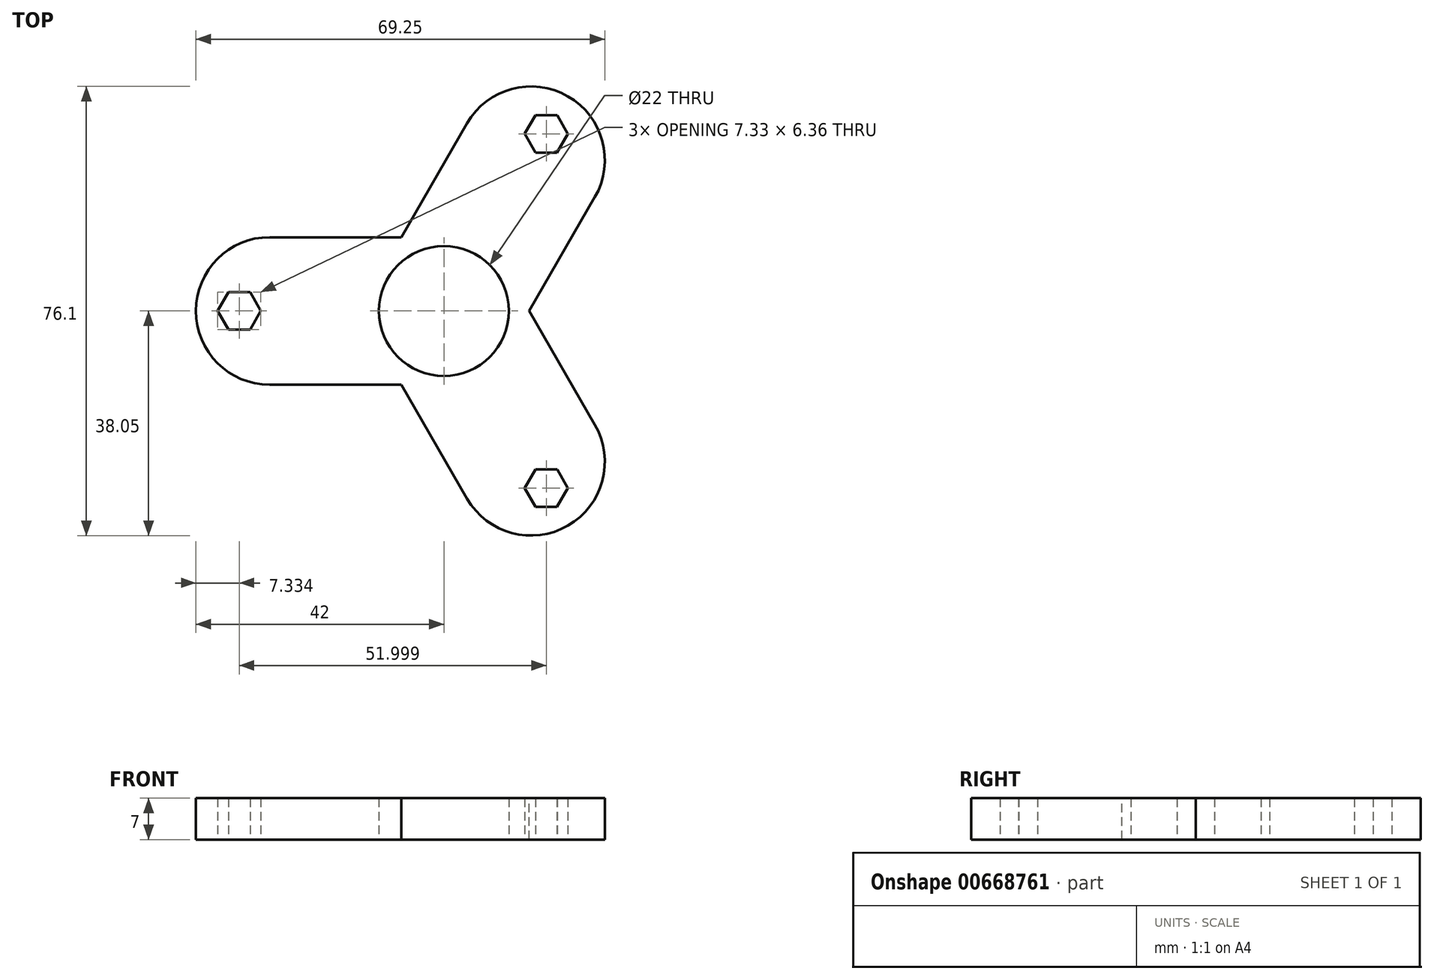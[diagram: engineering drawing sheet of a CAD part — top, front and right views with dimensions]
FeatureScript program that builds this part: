
annotation { "Feature Type Name" : "Feature", "Feature Type Description" : "" }
export const myFeature = defineFeature(function(context is Context, id is Id, definition is map)
    precondition{}
    {
        {
            var Q0;
            Q0=qCreatedBy(makeId("Front.planeOp"),FACE);
            var sketch = newSketch(context, id + "F0", { "sketchPlane" : qUnion([Q0])});
            skLineSegment(sketch, "E0", {"start": v(0, 0) * mm, "end": v(0, 6.18) * mm});
            skSolve(sketch);
        }
        {
            var Q0;
            Q0=qCreatedBy(makeId("Top.planeOp"),FACE);
            var sketch = newSketch(context, id + "F1", { "sketchPlane" : qUnion([Q0])});
            skArc(sketch, "E1", {"start": v(0, 11) * mm, "mid": v(-11, 0) * mm, "end": v(0, -11) * mm});
            skLineSegment(sketch, "E2", {"start": v(0, 56.07) * mm, "end": v(0, 11) * mm, "construction": true});
            skLineSegment(sketch, "E3", {"start": v(-42, 36.78) * mm, "end": v(-42, -48.45) * mm, "construction": true});
            skArc(sketch, "E4", {"start": v(-29.5, 12.5) * mm, "mid": v(-42, 0) * mm, "end": v(-29.5, -12.5) * mm});
            skLineSegment(sketch, "E5", {"start": v(0, 12.5) * mm, "end": v(-29.5, 12.5) * mm});
            skLineSegment(sketch, "E6", {"start": v(0, -12.5) * mm, "end": v(-29.5, -12.5) * mm});
            skLineSegment(sketch, "E7", {"start": v(0, 12.5) * mm, "end": v(0, 11) * mm});
            skLineSegment(sketch, "E8.trimOffspring", {"start": v(0, -11) * mm, "end": v(0, -55.82) * mm, "construction": true});
            skLineSegment(sketch, "E9.trimOffspring", {"start": v(0, -11) * mm, "end": v(0, -12.5) * mm});
            skPoint(sketch, "E10.endSnap0", {"position": v(-11, 0) * mm});
            skPoint(sketch, "E11", {"position": v(-34.67, 0) * mm});
            skCircle(sketch, "E12.cCircle", {"center": v(-34.67, 0) * mm, "radius": 3.17 * mm, "construction": true});
            skLineSegment(sketch, "E12.0", {"start": v(-36.5, -3.17) * mm, "end": v(-38.33, 0) * mm});
            skLineSegment(sketch, "E12.1", {"start": v(-38.33, 0) * mm, "end": v(-36.5, 3.18) * mm});
            skLineSegment(sketch, "E12.2", {"start": v(-36.5, 3.18) * mm, "end": v(-32.83, 3.17) * mm});
            skLineSegment(sketch, "E12.3", {"start": v(-32.83, 3.17) * mm, "end": v(-31, 0) * mm});
            skLineSegment(sketch, "E12.4", {"start": v(-31, 0) * mm, "end": v(-32.84, -3.18) * mm});
            skLineSegment(sketch, "E12.5", {"start": v(-32.84, -3.18) * mm, "end": v(-36.5, -3.17) * mm});
            skPoint(sketch, "E12.0.midPoint", {"position": v(-37.42, -1.58) * mm});
            skPoint(sketch, "E13", {"position": v(-17.17, 0) * mm});
            skLineSegment(sketch, "E14", {"start": v(-20345.58, -35023.95) * mm, "end": v(-35.38, 3.1) * mm});
            skPoint(sketch, "E14.startSnap0", {"position": v(-42, -5.83) * mm});
            skPoint(sketch, "E15.orphan", {"position": v(-40.56, -5.83) * mm});
            skPoint(sketch, "E16.trimOffspring.end.orphan", {"position": v(-13.5, 0.02) * mm});
            skPoint(sketch, "E17.1.start.orphan", {"position": v(-20.83, -0.02) * mm});
            skPoint(sketch, "E18.orphan", {"position": v(-46.75, -4.43) * mm});
            skPoint(sketch, "E19.end.orphan", {"position": v(-36.26, -10.52) * mm});
            skPoint(sketch, "E19.start.orphan", {"position": v(-9.63, -12.5) * mm});
            skPoint(sketch, "E20.MirrorCS.start.orphan", {"position": v(-61.7, 17.7) * mm});
            skSolve(sketch);
        }
        {
            var Q0;
            Q0=makeQuery(id+"F1.imprint","IMPRINT",FACE,{"disambiguationData":[TD([[makeQuery(id+"F1.imprint","IMPRINT",EDGE,{"derivedFrom":sQuery(id+"F1.wireOp",EDGE,"E1")}),-1.0]])]});
            extrude(context, id + "F2", {"entities" : qUnion([Q0]), "depth" : 7 * mm, "offsetDistance" : 25 * mm});
        }
        {
            var Q0;
            Q0=makeQuery(id+"F2.opExtrude","SWEPT_BODY",BODY,{"disambiguationData":[OSD([sQuery(id+"F1.wireOp",EDGE,"E1"),sQuery(id+"F1.wireOp",EDGE,"E4"),sQuery(id+"F1.wireOp",EDGE,"E5"),sQuery(id+"F1.wireOp",EDGE,"E6"),sQuery(id+"F1.wireOp",EDGE,"E7"),sQuery(id+"F1.wireOp",EDGE,"E9.trimOffspring"),sQuery(id+"F1.wireOp",EDGE,"E12.0"),sQuery(id+"F1.wireOp",EDGE,"E12.1"),sQuery(id+"F1.wireOp",EDGE,"E12.2"),sQuery(id+"F1.wireOp",EDGE,"E12.3"),sQuery(id+"F1.wireOp",EDGE,"E12.4"),sQuery(id+"F1.wireOp",EDGE,"E12.5"),sQuery(id+"F1.wireOp",EDGE,"E17.0"),sQuery(id+"F1.wireOp",EDGE,"E17.1"),sQuery(id+"F1.wireOp",EDGE,"E17.2"),sQuery(id+"F1.wireOp",EDGE,"E17.3"),sQuery(id+"F1.wireOp",EDGE,"E17.4"),sQuery(id+"F1.wireOp",EDGE,"E17.5")])]});
            var Q1;
            Q1=sQuery(id+"F0.wireOp",EDGE,"E0");
            circularPattern(context, id + "F3", {"operationType" : NewBodyOperationType.ADD, "entities" : qUnion([Q0]), "axis" : qUnion([Q1]), "angle" : 240 * degree, "instanceCount" : 3, "equalSpace" : true});
        }
    });
